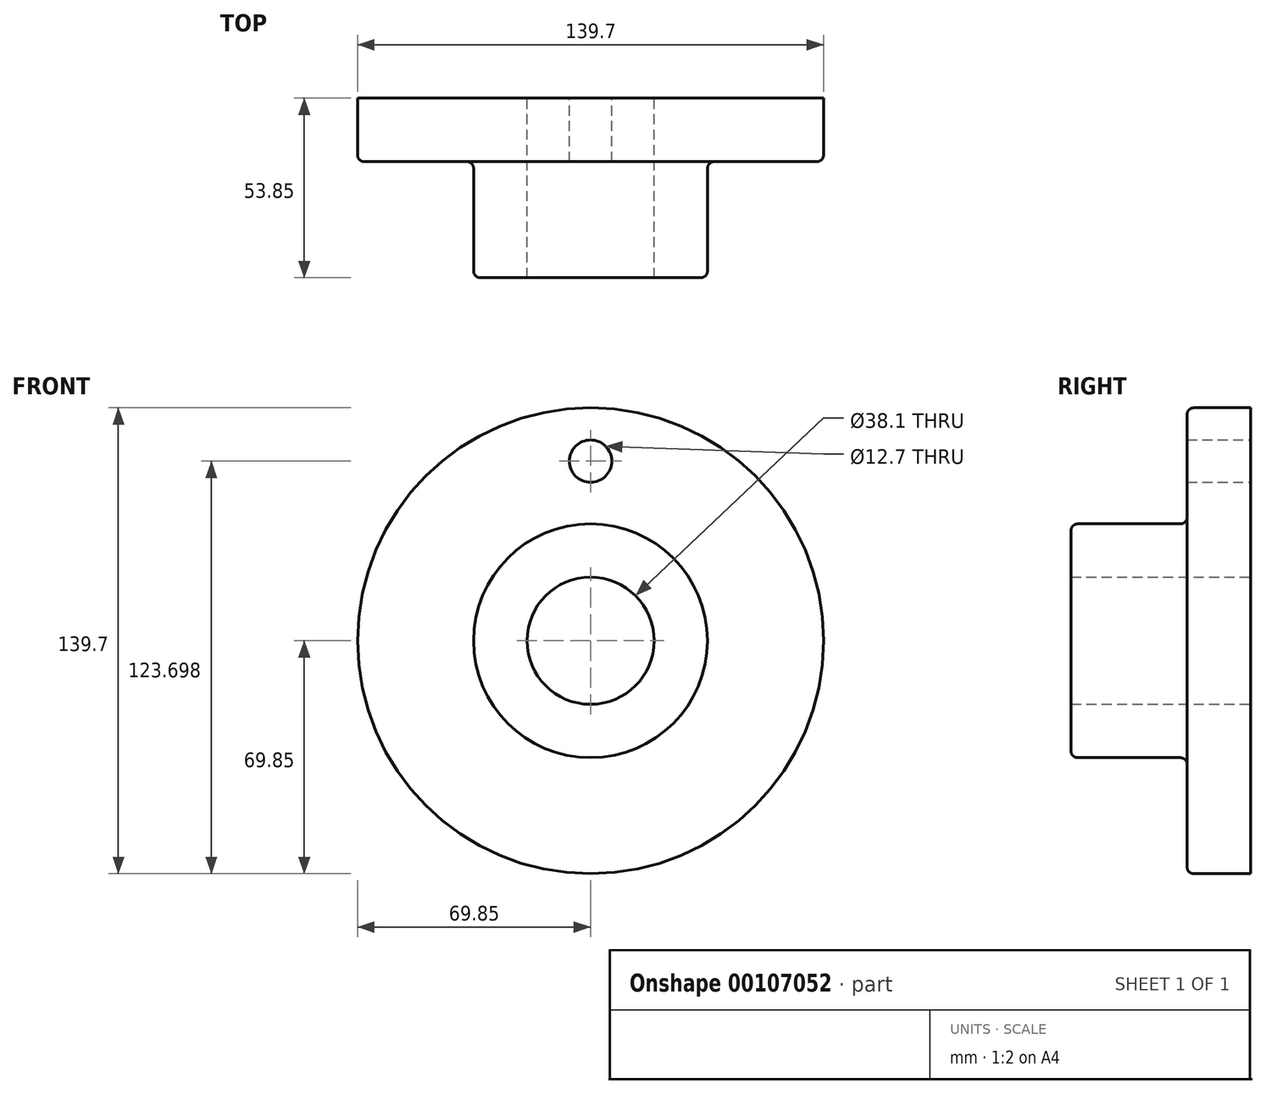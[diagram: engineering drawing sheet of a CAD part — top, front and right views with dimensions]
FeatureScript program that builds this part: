
annotation { "Feature Type Name" : "Feature", "Feature Type Description" : "" }
export const myFeature = defineFeature(function(context is Context, id is Id, definition is map)
    precondition{}
    {
        {
            var Q0;
            Q0=qCreatedBy(makeId("Right.planeOp"),FACE);
            var sketch = newSketch(context, id + "F0", { "sketchPlane" : qUnion([Q0])});
            skLineSegment(sketch, "E0", {"start": v(0, 0) * mm, "end": v(-53.85, 0) * mm, "construction": true});
            skLineSegment(sketch, "E1", {"start": v(0, 19.05) * mm, "end": v(-53.85, 19.05) * mm});
            skLineSegment(sketch, "E2", {"start": v(-53.85, 19.05) * mm, "end": v(-53.85, 35.05) * mm});
            skLineSegment(sketch, "E3", {"start": v(-53.85, 35.05) * mm, "end": v(-19.05, 35.05) * mm});
            skLineSegment(sketch, "E4", {"start": v(-19.05, 35.05) * mm, "end": v(-19.05, 69.85) * mm});
            skLineSegment(sketch, "E5", {"start": v(-19.05, 69.85) * mm, "end": v(0, 69.85) * mm});
            skLineSegment(sketch, "E6", {"start": v(0, 69.85) * mm, "end": v(0, 19.05) * mm});
            skSolve(sketch);
        }
        {
            var Q0;
            Q0 = qSketchRegion(id + "F0", true);
            var Q1;
            Q1 = qSketchRegion(id + "F2", true);
            var Q2;
            Q2=sQuery(id+"F0.wireOp",EDGE,"E0");
            revolve(context, id + "F1", {"entities" : qUnion([Q0, Q1]), "axis" : qUnion([Q2]), "revolveType" : RevolveType.FULL});
        }
        {
            var Q0;
            Q0=qCreatedBy(makeId("Front.planeOp"),FACE);
            var sketch = newSketch(context, id + "F2", { "sketchPlane" : qUnion([Q0])});
            skCircle(sketch, "E7", {"center": v(0, 265.2) * mm, "radius": 63.5 * mm});
            skCircle(sketch, "E8", {"center": v(0, 53.85) * mm, "radius": 6.35 * mm});
            skCircle(sketch, "E9", {"center": v(0, 0) * mm, "radius": 53.85 * mm, "construction": true});
            skSolve(sketch);
        }
        {
            var Q0;
            Q0 = qSketchRegion(id + "F2", true);
            extrude(context, id + "F3", {"entities" : qUnion([Q0]), "operationType" : NewBodyOperationType.REMOVE, "endBound" : BoundingType.THROUGH_ALL, "depth" : 25.4 * mm});
        }
        {
            var Q0;
            Q0=makeQuery(id+"F1.opRevolve","SWEPT_EDGE",EDGE,{"disambiguationData":[OSD([sQuery(id+"F0.wireOp",EDGE,"E4"),sQuery(id+"F0.wireOp",EDGE,"E5")])]});
            var Q1;
            Q1=makeQuery(id+"F1.opRevolve","SWEPT_EDGE",EDGE,{"disambiguationData":[OSD([sQuery(id+"F0.wireOp",EDGE,"E3"),sQuery(id+"F0.wireOp",EDGE,"E4")])]});
            var Q2;
            Q2=makeQuery(id+"F1.opRevolve","SWEPT_EDGE",EDGE,{"disambiguationData":[OSD([sQuery(id+"F0.wireOp",EDGE,"E2"),sQuery(id+"F0.wireOp",EDGE,"E3")])]});
            fillet(context, id + "F4", {"entities" : qUnion([Q0, Q1, Q2]), "radius" : 2 * mm, "tangentPropagation" : true, "allowEdgeOverflow" : false});
        }
    });
